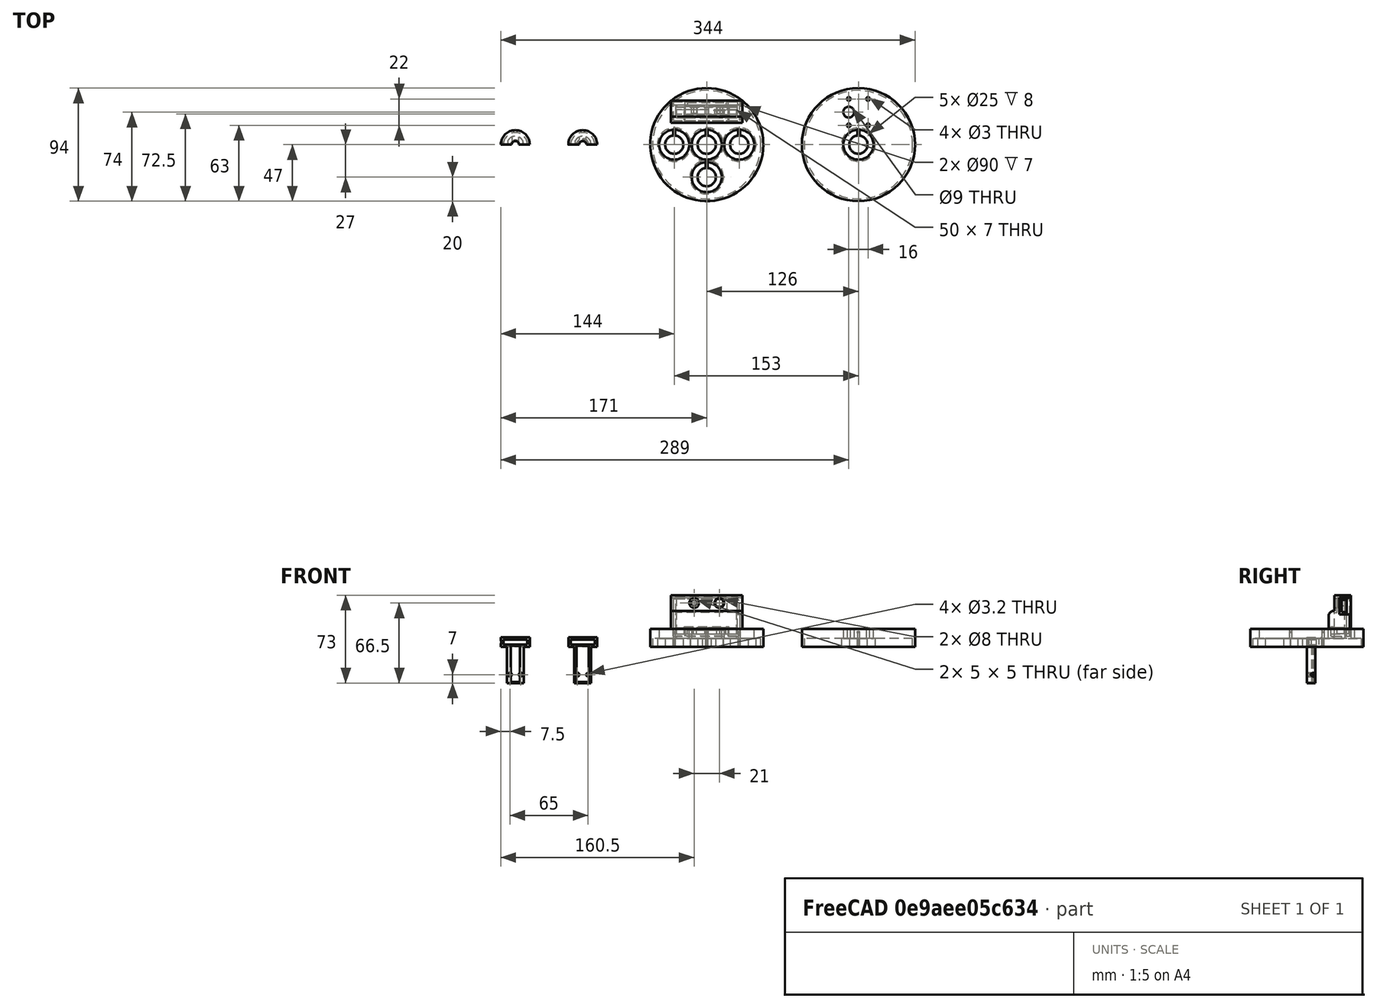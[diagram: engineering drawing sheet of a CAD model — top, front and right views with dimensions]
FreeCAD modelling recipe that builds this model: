
FCSTD DOCUMENT  (FreeCAD 0.21RUnknown)
Label: lidcup
License: All rights reserved
LicenseURL: https://en.wikipedia.org/wiki/All_rights_reserved
objects: PartDesign::SubtractiveCylinder×35, PartDesign::SubtractiveBox×18, PartDesign::AdditiveBox×17, PartDesign::AdditiveCylinder×13, PartDesign::Body×8, PartDesign::Fillet×1
note: 176 computed .brp shape members not serialized (recipe doc carries the construction recipe); baked Part::Feature solids carry a one-line shape summary decoded from their .brp

FEATURE [PartDesign::AdditiveCylinder] Cylinder
  Angle = 360
  AttacherType = Attacher::AttachEngine3D
  FirstAngle = 0
  Height = 15
  MapMode = 5
  Radius = 47
  SecondAngle = 0
  Support = -> [XY_Plane]
FEATURE [PartDesign::SubtractiveCylinder] Cylinder001
  Angle = 360
  AttacherType = Attacher::AttachEngine3D
  BaseFeature = -> Cylinder
  FirstAngle = 0
  Height = 7
  Radius = 45
  SecondAngle = 0
FEATURE [PartDesign::AdditiveCylinder] Cylinder003
  Angle = 360
  AttacherType = Attacher::AttachEngine3D
  BaseFeature = -> Cylinder001
  FirstAngle = 0
  Height = 10
  MapMode = 5
  Radius = 14
  SecondAngle = 0
  Support = -> [XY_Plane]
FEATURE [PartDesign::SubtractiveCylinder] Cylinder002
  Angle = 360
  AttacherType = Attacher::AttachEngine3D
  AttachmentOffset = pos=(0,0,7) rot=(0,0,1;0rad)
  BaseFeature = -> Cylinder003
  FirstAngle = 0
  Height = 8
  MapMode = 5
  Placement = pos=(0,0,7) rot=(0,0,1;0rad)
  Radius = 12.5
  SecondAngle = 0
  Support = -> [XY_Plane]
FEATURE [PartDesign::SubtractiveCylinder] Cylinder004
  Angle = 360
  AttacherType = Attacher::AttachEngine3D
  BaseFeature = -> Cylinder002
  FirstAngle = 0
  Height = 10
  Radius = 7.6
  SecondAngle = 0
FEATURE [PartDesign::SubtractiveBox] Box
  AttacherType = Attacher::AttachEngine3D
  AttachmentOffset = pos=(-0.75,0,0) rot=(0,0,1;0rad)
  BaseFeature = -> Cylinder004
  Height = 13
  Length = 1.5
  MapMode = 5
  Placement = pos=(-0.75,0,0) rot=(0,0,1;0rad)
  Support = -> [XY_Plane]
  Width = 13.3
FEATURE [PartDesign::SubtractiveCylinder] Cylinder005
  Angle = 360
  AttacherType = Attacher::AttachEngine3D
  AttachmentOffset = pos=(-8,38,0) rot=(0,0,1;0rad)
  BaseFeature = -> Box
  FirstAngle = 0
  Height = 15
  MapMode = 5
  Placement = pos=(-8,38,0) rot=(0,0,1;0rad)
  Radius = 1.5
  SecondAngle = 0
  Support = -> [XY_Plane]
FEATURE [PartDesign::SubtractiveCylinder] Cylinder006
  Angle = 360
  AttacherType = Attacher::AttachEngine3D
  AttachmentOffset = pos=(-8,16,0) rot=(0,0,1;0rad)
  BaseFeature = -> Cylinder005
  FirstAngle = 0
  Height = 15
  MapMode = 5
  Placement = pos=(-8,16,0) rot=(0,0,1;0rad)
  Radius = 1.5
  SecondAngle = 0
  Support = -> [XY_Plane]
FEATURE [PartDesign::SubtractiveCylinder] Cylinder007
  Angle = 360
  AttacherType = Attacher::AttachEngine3D
  AttachmentOffset = pos=(8,38,0) rot=(0,0,1;0rad)
  BaseFeature = -> Cylinder006
  FirstAngle = 0
  Height = 15
  MapMode = 5
  Placement = pos=(8,38,0) rot=(0,0,1;0rad)
  Radius = 1.5
  SecondAngle = 0
  Support = -> [XY_Plane]
FEATURE [PartDesign::SubtractiveCylinder] Cylinder008
  Angle = 360
  AttacherType = Attacher::AttachEngine3D
  AttachmentOffset = pos=(8,16,0) rot=(0,0,1;0rad)
  BaseFeature = -> Cylinder007
  FirstAngle = 0
  Height = 15
  MapMode = 5
  Placement = pos=(8,16,0) rot=(0,0,1;0rad)
  Radius = 1.5
  SecondAngle = 0
  Support = -> [XY_Plane]
FEATURE [PartDesign::SubtractiveCylinder] Cylinder009
  Angle = 360
  AttacherType = Attacher::AttachEngine3D
  AttachmentOffset = pos=(-8,27,0) rot=(0,0,1;0rad)
  BaseFeature = -> Cylinder008
  FirstAngle = 0
  Height = 15
  MapMode = 5
  Placement = pos=(-8,27,0) rot=(0,0,1;0rad)
  Radius = 4.5
  SecondAngle = 0
  Support = -> [XY_Plane]
FEATURE [PartDesign::Body] Body  label="Cup"
  Group = -> [Cylinder,Cylinder001,Cylinder003,Cylinder002,Cylinder004,Box,Cylinder005,Cylinder006,Cylinder007,Cylinder008,Cylinder009]
  Origin = -> Origin
  Tip = -> Cylinder009
FEATURE [PartDesign::AdditiveCylinder] Cylinder010
  Angle = 360
  AttacherType = Attacher::AttachEngine3D
  FirstAngle = 0
  Height = 15
  MapMode = 5
  Radius = 47
  SecondAngle = 0
  Support = -> [XY_Plane001]
FEATURE [PartDesign::SubtractiveCylinder] Cylinder011
  Angle = 360
  AttacherType = Attacher::AttachEngine3D
  BaseFeature = -> Cylinder010
  FirstAngle = 0
  Height = 7
  MapMode = 5
  Radius = 45
  SecondAngle = 0
  Support = -> [XY_Plane001]
FEATURE [PartDesign::AdditiveBox] Box002
  AttacherType = Attacher::AttachEngine3D
  Height = 1.5
  Length = 50
  MapMode = 5
  Support = -> [XY_Plane002]
  Width = 30
FEATURE [PartDesign::AdditiveBox] Box003
  AttacherType = Attacher::AttachEngine3D
  AttachmentOffset = pos=(42,18,0) rot=(0,0,1;0rad)
  BaseFeature = -> Box002
  Height = 4
  Length = 10
  MapMode = 5
  Placement = pos=(42,18,0) rot=(0,0,1;0rad)
  Support = -> [XY_Plane002]
  Width = 10
FEATURE [PartDesign::AdditiveCylinder] Cylinder017
  Angle = 360
  AttacherType = Attacher::AttachEngine3D
  BaseFeature = -> Cylinder011
  FirstAngle = 0
  Height = 10
  MapMode = 5
  Radius = 14
  SecondAngle = 0
  Support = -> [XY_Plane001]
FEATURE [PartDesign::SubtractiveCylinder] Cylinder013
  Angle = 360
  AttacherType = Attacher::AttachEngine3D
  AttachmentOffset = pos=(0,0,7) rot=(0,0,1;0rad)
  BaseFeature = -> Cylinder017
  FirstAngle = 0
  Height = 8
  MapMode = 5
  Placement = pos=(0,0,7) rot=(0,0,1;0rad)
  Radius = 12.5
  SecondAngle = 0
  Support = -> [XY_Plane001]
FEATURE [PartDesign::SubtractiveCylinder] Cylinder014
  Angle = 360
  AttacherType = Attacher::AttachEngine3D
  BaseFeature = -> Cylinder013
  FirstAngle = 0
  Height = 10
  MapMode = 5
  Radius = 7.6
  SecondAngle = 0
  Support = -> [XY_Plane001]
FEATURE [PartDesign::SubtractiveBox] Box001
  AttacherType = Attacher::AttachEngine3D
  AttachmentOffset = pos=(-0.75,0,0) rot=(0,0,1;0rad)
  BaseFeature = -> Cylinder014
  Height = 13
  Length = 1.5
  MapMode = 5
  Placement = pos=(-0.75,0,0) rot=(0,0,1;0rad)
  Support = -> [XY_Plane001]
  Width = 13.3
FEATURE [PartDesign::AdditiveCylinder] Cylinder015
  Angle = 360
  AttacherType = Attacher::AttachEngine3D
  AttachmentOffset = pos=(-27,0,0) rot=(0,0,1;0rad)
  BaseFeature = -> Box001
  FirstAngle = 0
  Height = 10
  MapMode = 5
  Placement = pos=(-27,0,0) rot=(0,0,1;0rad)
  Radius = 14
  SecondAngle = 0
  Support = -> [XY_Plane001]
FEATURE [PartDesign::AdditiveBox] Box004
  AttacherType = Attacher::AttachEngine3D
  AttachmentOffset = pos=(33,23,0) rot=(0,0,1;0rad)
  BaseFeature = -> Box003
  Height = 7
  Length = 5
  MapMode = 5
  Placement = pos=(33,23,0) rot=(0,0,1;0rad)
  Support = -> [XY_Plane002]
  Width = 5
FEATURE [PartDesign::AdditiveBox] Box005
  AttacherType = Attacher::AttachEngine3D
  AttachmentOffset = pos=(12,23,0) rot=(0,0,1;0rad)
  BaseFeature = -> Box004
  Height = 7
  Length = 5
  MapMode = 5
  Placement = pos=(12,23,0) rot=(0,0,1;0rad)
  Support = -> [XY_Plane002]
  Width = 5
FEATURE [PartDesign::AdditiveBox] Box006
  AttacherType = Attacher::AttachEngine3D
  AttachmentOffset = pos=(7,0,0) rot=(0,0,1;0rad)
  BaseFeature = -> Box005
  Height = 8
  Length = 7
  MapMode = 5
  Placement = pos=(7,0,0) rot=(0,0,1;0rad)
  Support = -> [XY_Plane002]
  Width = 5
FEATURE [PartDesign::AdditiveBox] Box007
  AttacherType = Attacher::AttachEngine3D
  AttachmentOffset = pos=(16.5,0,0) rot=(0,0,1;0rad)
  BaseFeature = -> Box006
  Height = 8
  Length = 7
  MapMode = 5
  Placement = pos=(16.5,0,0) rot=(0,0,1;0rad)
  Support = -> [XY_Plane002]
  Width = 5
FEATURE [PartDesign::AdditiveBox] Box008
  AttacherType = Attacher::AttachEngine3D
  AttachmentOffset = pos=(26.5,0,0) rot=(0,0,1;0rad)
  BaseFeature = -> Box007
  Height = 8
  Length = 7
  MapMode = 5
  Placement = pos=(26.5,0,0) rot=(0,0,1;0rad)
  Support = -> [XY_Plane002]
  Width = 5
FEATURE [PartDesign::AdditiveBox] Box009
  AttacherType = Attacher::AttachEngine3D
  AttachmentOffset = pos=(36,0,0) rot=(0,0,1;0rad)
  BaseFeature = -> Box008
  Height = 8
  Length = 7
  MapMode = 5
  Placement = pos=(36,0,0) rot=(0,0,1;0rad)
  Support = -> [XY_Plane002]
  Width = 5
FEATURE [PartDesign::SubtractiveCylinder] Cylinder019
  Angle = 360
  AttacherType = Attacher::AttachEngine3D
  AttachmentOffset = pos=(-27,0,7) rot=(0,0,1;0rad)
  BaseFeature = -> Cylinder015
  FirstAngle = 0
  Height = 8
  MapMode = 5
  Placement = pos=(-27,0,7) rot=(0,0,1;0rad)
  Radius = 12.5
  SecondAngle = 0
  Support = -> [XY_Plane001]
FEATURE [PartDesign::SubtractiveCylinder] Cylinder020
  Angle = 360
  AttacherType = Attacher::AttachEngine3D
  AttachmentOffset = pos=(-27,0,0) rot=(0,0,1;0rad)
  BaseFeature = -> Cylinder019
  FirstAngle = 0
  Height = 10
  MapMode = 5
  Placement = pos=(-27,0,0) rot=(0,0,1;0rad)
  Radius = 7.6
  SecondAngle = 0
  Support = -> [XY_Plane001]
FEATURE [PartDesign::SubtractiveBox] Box012
  AttacherType = Attacher::AttachEngine3D
  AttachmentOffset = pos=(-27.75,0,0) rot=(0,0,1;0rad)
  BaseFeature = -> Cylinder020
  Height = 13
  Length = 1.5
  MapMode = 5
  Placement = pos=(-27.75,0,0) rot=(0,0,1;0rad)
  Support = -> [XY_Plane001]
  Width = 13.3
FEATURE [PartDesign::AdditiveCylinder] Cylinder016
  Angle = 360
  AttacherType = Attacher::AttachEngine3D
  AttachmentOffset = pos=(27,0,0) rot=(0,0,1;0rad)
  BaseFeature = -> Box012
  FirstAngle = 0
  Height = 10
  MapMode = 5
  Placement = pos=(27,0,0) rot=(0,0,1;0rad)
  Radius = 14
  SecondAngle = 0
  Support = -> [XY_Plane001]
FEATURE [PartDesign::SubtractiveCylinder] Cylinder021
  Angle = 360
  AttacherType = Attacher::AttachEngine3D
  AttachmentOffset = pos=(27,0,7) rot=(0,0,1;0rad)
  BaseFeature = -> Cylinder016
  FirstAngle = 0
  Height = 8
  MapMode = 5
  Placement = pos=(27,0,7) rot=(0,0,1;0rad)
  Radius = 12.5
  SecondAngle = 0
  Support = -> [XY_Plane001]
FEATURE [PartDesign::SubtractiveCylinder] Cylinder022
  Angle = 360
  AttacherType = Attacher::AttachEngine3D
  AttachmentOffset = pos=(27,0,0) rot=(0,0,1;0rad)
  BaseFeature = -> Cylinder021
  FirstAngle = 0
  Height = 10
  MapMode = 5
  Placement = pos=(27,0,0) rot=(0,0,1;0rad)
  Radius = 7.6
  SecondAngle = 0
  Support = -> [XY_Plane001]
FEATURE [PartDesign::SubtractiveBox] Box013
  AttacherType = Attacher::AttachEngine3D
  AttachmentOffset = pos=(26.25,0,0) rot=(0,0,1;0rad)
  BaseFeature = -> Cylinder022
  Height = 13
  Length = 1.5
  MapMode = 5
  Placement = pos=(26.25,0,0) rot=(0,0,1;0rad)
  Support = -> [XY_Plane001]
  Width = 13.3
FEATURE [PartDesign::AdditiveCylinder] Cylinder018
  Angle = 360
  AttacherType = Attacher::AttachEngine3D
  AttachmentOffset = pos=(0,-27,0) rot=(0,0,1;0rad)
  BaseFeature = -> Box013
  FirstAngle = 0
  Height = 10
  MapMode = 5
  Placement = pos=(0,-27,0) rot=(0,0,1;0rad)
  Radius = 14
  SecondAngle = 0
  Support = -> [XY_Plane001]
FEATURE [PartDesign::SubtractiveCylinder] Cylinder023
  Angle = 360
  AttacherType = Attacher::AttachEngine3D
  AttachmentOffset = pos=(0,-27,7) rot=(0,0,1;0rad)
  BaseFeature = -> Cylinder018
  FirstAngle = 0
  Height = 8
  MapMode = 5
  Placement = pos=(0,-27,7) rot=(0,0,1;0rad)
  Radius = 12.5
  SecondAngle = 0
  Support = -> [XY_Plane001]
FEATURE [PartDesign::SubtractiveCylinder] Cylinder024
  Angle = 360
  AttacherType = Attacher::AttachEngine3D
  AttachmentOffset = pos=(0,-27,0) rot=(0,0,1;0rad)
  BaseFeature = -> Cylinder023
  FirstAngle = 0
  Height = 10
  MapMode = 5
  Placement = pos=(0,-27,0) rot=(0,0,1;0rad)
  Radius = 7.6
  SecondAngle = 0
  Support = -> [XY_Plane001]
FEATURE [PartDesign::SubtractiveBox] Box014
  AttacherType = Attacher::AttachEngine3D
  AttachmentOffset = pos=(-0.75,-27,0) rot=(0,0,1;0rad)
  BaseFeature = -> Cylinder024
  Height = 13
  Length = 1.5
  MapMode = 5
  Placement = pos=(-0.75,-27,0) rot=(0,0,1;0rad)
  Support = -> [XY_Plane001]
  Width = 13.3
FEATURE [PartDesign::SubtractiveBox] Box010
  AttacherType = Attacher::AttachEngine3D
  AttachmentOffset = pos=(-28,20,9) rot=(0,0,1;0rad)
  BaseFeature = -> Box014
  Height = 6
  Length = 56
  MapMode = 5
  Placement = pos=(-28,20,9) rot=(0,0,1;0rad)
  Support = -> [XY_Plane001]
  Width = 16
FEATURE [PartDesign::SubtractiveBox] Box011
  AttacherType = Attacher::AttachEngine3D
  AttachmentOffset = pos=(-25,22,0) rot=(0,0,1;0rad)
  BaseFeature = -> Box010
  Height = 10
  Length = 50
  MapMode = 5
  Placement = pos=(-25,22,0) rot=(0,0,1;0rad)
  Support = -> [XY_Plane001]
  Width = 7
FEATURE [PartDesign::Body] Body001  label="Cup 4"
  Group = -> [Cylinder010,Cylinder011,Cylinder017,Cylinder013,Cylinder014,Box001,Cylinder015,Cylinder019,Cylinder020,Box012,Cylinder016,Cylinder021,Cylinder022,Box013,Cylinder018,Cylinder023,Cylinder024,Box014,Box010,Box011]
  Origin = -> Origin001
  Placement = pos=(-126,0,0) rot=(0,0,1;0rad)
  Tip = -> Box011
FEATURE [PartDesign::AdditiveCylinder] Cylinder025
  Angle = 360
  AttacherType = Attacher::AttachEngine3D
  FirstAngle = 0
  Height = 8
  MapMode = 5
  Radius = 12
  SecondAngle = 0
  Support = -> [XY_Plane003]
FEATURE [PartDesign::AdditiveCylinder] Cylinder026
  Angle = 360
  AttacherType = Attacher::AttachEngine3D
  AttachmentOffset = pos=(0,0,-30) rot=(0,0,1;0rad)
  BaseFeature = -> Cylinder025
  FirstAngle = 0
  Height = 30
  MapMode = 5
  Placement = pos=(0,0,-30) rot=(0,0,1;0rad)
  Radius = 7
  SecondAngle = 0
  Support = -> [XY_Plane003]
FEATURE [PartDesign::SubtractiveBox] Box015
  AttacherType = Attacher::AttachEngine3D
  AttachmentOffset = pos=(-12,-12,-30) rot=(0,0,1;0rad)
  BaseFeature = -> Cylinder026
  Height = 38
  Length = 24
  MapMode = 5
  Placement = pos=(-12,-12,-30) rot=(0,0,1;0rad)
  Support = -> [XY_Plane003]
  Width = 12
FEATURE [PartDesign::SubtractiveCylinder] Cylinder027
  Angle = 360
  AttacherType = Attacher::AttachEngine3D
  AttachmentOffset = pos=(0,0,-29) rot=(0,0,1;0rad)
  BaseFeature = -> Box015
  FirstAngle = 0
  Height = 30
  MapMode = 5
  Placement = pos=(0,0,-29) rot=(0,0,1;0rad)
  Radius = 5
  SecondAngle = 0
  Support = -> [XY_Plane003]
FEATURE [PartDesign::SubtractiveCylinder] Cylinder028
  Angle = 360
  AttacherType = Attacher::AttachEngine3D
  AttachmentOffset = pos=(0,0,-30) rot=(0,0,1;0rad)
  BaseFeature = -> Cylinder027
  FirstAngle = 0
  Height = 1
  MapMode = 5
  Placement = pos=(0,0,-30) rot=(0,0,1;0rad)
  Radius = 4.5
  SecondAngle = 0
  Support = -> [XY_Plane003]
FEATURE [PartDesign::SubtractiveCylinder] Cylinder032
  Angle = 360
  AttacherType = Attacher::AttachEngine3D
  AttachmentOffset = pos=(0,0,1) rot=(0,0,1;0rad)
  BaseFeature = -> Cylinder028
  FirstAngle = 0
  Height = 1
  MapMode = 5
  Placement = pos=(0,0,1) rot=(0,0,1;0rad)
  Radius = 4.5
  SecondAngle = 0
  Support = -> [XY_Plane003]
FEATURE [PartDesign::SubtractiveCylinder] Cylinder029
  Angle = 360
  AttacherType = Attacher::AttachEngine3D
  AttachmentOffset = pos=(0,0,2) rot=(0,0,1;0rad)
  BaseFeature = -> Cylinder032
  FirstAngle = 0
  Height = 4
  MapMode = 5
  Placement = pos=(0,0,2) rot=(0,0,1;0rad)
  Radius = 10
  SecondAngle = 0
  Support = -> [XY_Plane003]
FEATURE [PartDesign::SubtractiveCylinder] Cylinder030
  Angle = 360
  AttacherType = Attacher::AttachEngine3D
  AttachmentOffset = pos=(0,0,6) rot=(0,0,1;0rad)
  BaseFeature = -> Cylinder029
  FirstAngle = 0
  Height = 2
  MapMode = 5
  Placement = pos=(0,0,6) rot=(0,0,1;0rad)
  Radius = 3
  SecondAngle = 0
  Support = -> [XY_Plane003]
FEATURE [PartDesign::SubtractiveCylinder] Cylinder031
  Angle = 360
  AttacherType = Attacher::AttachEngine3D
  AttachmentOffset = pos=(0,4,-12) rot=(0,0,1;0rad)
  BaseFeature = -> Cylinder030
  FirstAngle = 0
  Height = 10
  MapMode = 5
  Placement = pos=(-12,3.6e-15,4) rot=(0.57735,0.57735,0.57735;2.0944rad)
  Radius = 1.4
  SecondAngle = 0
  Support = -> [YZ_Plane003]
FEATURE [PartDesign::AdditiveBox] Box016
  AttacherType = Attacher::AttachEngine3D
  AttachmentOffset = pos=(9,0,-2) rot=(0,0,1;0rad)
  BaseFeature = -> Box009
  Height = 2
  Length = 32
  MapMode = 5
  Placement = pos=(9,0,-2) rot=(0,0,1;0rad)
  Support = -> [XY_Plane002]
  Width = 3
FEATURE [PartDesign::Body] Body002  label="PCB"
  Group = -> [Box002,Box003,Box004,Box005,Box006,Box007,Box008,Box009,Box016]
  Origin = -> Origin002
  Placement = pos=(-151,33,11) rot=(1,0,0;1.5708rad)
  Tip = -> Box016
FEATURE [PartDesign::AdditiveBox] Box017
  AttacherType = Attacher::AttachEngine3D
  Height = 32
  Length = 55.2
  MapMode = 5
  Support = -> [XY_Plane004]
  Width = 2.5
FEATURE [PartDesign::SubtractiveBox] Box018
  AttacherType = Attacher::AttachEngine3D
  AttachmentOffset = pos=(9.5,0,0) rot=(0,0,1;0rad)
  BaseFeature = -> Box017
  Height = 7
  Length = 36
  MapMode = 5
  Placement = pos=(9.5,0,0) rot=(0,0,1;0rad)
  Support = -> [XY_Plane004]
  Width = 3
FEATURE [PartDesign::AdditiveBox] Box023
  AttacherType = Attacher::AttachEngine3D
  Height = 4
  Length = 55.2
  MapMode = 5
  Support = -> [XY_Plane005]
  Width = 13
FEATURE [PartDesign::AdditiveBox] Box024
  AttacherType = Attacher::AttachEngine3D
  AttachmentOffset = pos=(-2,-2,4) rot=(0,0,1;0rad)
  BaseFeature = -> Box023
  Height = 28
  Length = 59.2
  MapMode = 5
  Placement = pos=(-2,-2,4) rot=(0,0,1;0rad)
  Support = -> [XY_Plane005]
  Width = 17.5
FEATURE [PartDesign::SubtractiveBox] Box025
  AttacherType = Attacher::AttachEngine3D
  AttachmentOffset = pos=(9,0,0) rot=(0,0,1;0rad)
  BaseFeature = -> Box024
  Height = 6
  Length = 37
  MapMode = 5
  Placement = pos=(9,0,0) rot=(0,0,1;0rad)
  Support = -> [XY_Plane005]
  Width = 13
FEATURE [PartDesign::SubtractiveBox] Box026
  AttacherType = Attacher::AttachEngine3D
  AttachmentOffset = pos=(2,11,0) rot=(0,0,1;0rad)
  BaseFeature = -> Box025
  Height = 30.5
  Length = 51
  MapMode = 5
  Placement = pos=(2,11,0) rot=(0,0,1;0rad)
  Support = -> [XY_Plane005]
  Width = 2
FEATURE [PartDesign::SubtractiveBox] Box027
  AttacherType = Attacher::AttachEngine3D
  AttachmentOffset = pos=(2,3,5) rot=(0,0,1;0rad)
  BaseFeature = -> Box026
  Height = 12.5
  Length = 51
  MapMode = 5
  Placement = pos=(2,3,5) rot=(0,0,1;0rad)
  Support = -> [XY_Plane005]
  Width = 8
FEATURE [PartDesign::SubtractiveBox] Box028
  AttacherType = Attacher::AttachEngine3D
  AttachmentOffset = pos=(-2,-2,19) rot=(0,0,1;0rad)
  BaseFeature = -> Box027
  Height = 13
  Length = 59.2
  MapMode = 5
  Placement = pos=(-2,-2,19) rot=(0,0,1;0rad)
  Support = -> [XY_Plane005]
  Width = 5
FEATURE [PartDesign::SubtractiveBox] Box029
  AttacherType = Attacher::AttachEngine3D
  AttachmentOffset = pos=(2,5,17) rot=(0,0,1;0rad)
  BaseFeature = -> Box028
  Height = 13
  Length = 51
  MapMode = 5
  Placement = pos=(2,5,17) rot=(0,0,1;0rad)
  Support = -> [XY_Plane005]
  Width = 8
FEATURE [PartDesign::SubtractiveCylinder] Cylinder033
  Angle = 360
  AttacherType = Attacher::AttachEngine3D
  AttachmentOffset = pos=(17.1,25.5,-5) rot=(0,0,1;0rad)
  BaseFeature = -> Box029
  FirstAngle = 0
  Height = 3
  MapMode = 5
  Placement = pos=(17.1,5,25.5) rot=(1,0,0;1.5708rad)
  Radius = 4
  SecondAngle = 0
  Support = -> [XZ_Plane005]
FEATURE [PartDesign::SubtractiveCylinder] Cylinder034
  Angle = 360
  AttacherType = Attacher::AttachEngine3D
  AttachmentOffset = pos=(38.1,25.5,-5) rot=(0,0,1;0rad)
  BaseFeature = -> Cylinder033
  FirstAngle = 0
  Height = 3
  MapMode = 5
  Placement = pos=(38.1,5,25.5) rot=(1,0,0;1.5708rad)
  Radius = 4
  SecondAngle = 0
  Support = -> [XZ_Plane005]
FEATURE [PartDesign::SubtractiveBox] Box030
  AttacherType = Attacher::AttachEngine3D
  AttachmentOffset = pos=(53,7,16) rot=(0,0,1;0rad)
  BaseFeature = -> Cylinder034
  Height = 14
  Length = 5
  MapMode = 5
  Placement = pos=(53,7,16) rot=(0,0,1;0rad)
  Support = -> [XY_Plane005]
  Width = 8.5
FEATURE [PartDesign::SubtractiveBox] Box031
  AttacherType = Attacher::AttachEngine3D
  AttachmentOffset = pos=(0,13,4) rot=(0,0,1;0rad)
  BaseFeature = -> Box030
  Height = 25
  Length = 55.2
  MapMode = 5
  Placement = pos=(0,13,4) rot=(0,0,1;0rad)
  Support = -> [XY_Plane005]
  Width = 2.5
FEATURE [PartDesign::SubtractiveCylinder] Cylinder035
  Angle = 360
  AttacherType = Attacher::AttachEngine3D
  AttachmentOffset = pos=(4.5,-23,-7) rot=(0,0,1;0rad)
  BaseFeature = -> Cylinder031
  FirstAngle = 0
  Height = 7
  MapMode = 5
  Placement = pos=(4.5,7,-23) rot=(1,0,0;1.5708rad)
  Radius = 1.6
  SecondAngle = 0
  Support = -> [XZ_Plane003]
FEATURE [PartDesign::SubtractiveCylinder] Cylinder036
  Angle = 360
  AttacherType = Attacher::AttachEngine3D
  AttachmentOffset = pos=(-4.5,-23,-7) rot=(0,0,1;0rad)
  BaseFeature = -> Cylinder035
  FirstAngle = 0
  Height = 7
  MapMode = 5
  Placement = pos=(-4.5,7,-23) rot=(1,0,0;1.5708rad)
  Radius = 1.6
  SecondAngle = 0
  Support = -> [XZ_Plane003]
FEATURE [PartDesign::Body] Body003  label="Cotton Holder 10"
  Group = -> [Cylinder025,Cylinder026,Box015,Cylinder027,Cylinder028,Cylinder032,Cylinder029,Cylinder030,Cylinder031,Cylinder035,Cylinder036]
  Origin = -> Origin003
  Placement = pos=(-229,0,0) rot=(0,0,1;0rad)
  Tip = -> Cylinder036
FEATURE [PartDesign::AdditiveCylinder] Cylinder037
  Angle = 360
  AttacherType = Attacher::AttachEngine3D
  FirstAngle = 0
  Height = 5
  MapMode = 5
  Placement = pos=(0,0,0) rot=(1,0,0;1.5708rad)
  Radius = 3.75
  SecondAngle = 0
  Support = -> [XZ_Plane006]
FEATURE [PartDesign::AdditiveCylinder] Cylinder038
  Angle = 360
  AttacherType = Attacher::AttachEngine3D
  AttachmentOffset = pos=(0,0,-0.8) rot=(0,0,1;0rad)
  BaseFeature = -> Cylinder037
  FirstAngle = 0
  Height = 0.8
  MapMode = 5
  Placement = pos=(0,0.8,2e-16) rot=(1,0,0;1.5708rad)
  Radius = 4.4
  SecondAngle = 0
  Support = -> [XZ_Plane006]
FEATURE [PartDesign::Body] Body006  label="Button"
  Group = -> [Cylinder037,Cylinder038]
  Origin = -> Origin006
  Placement = pos=(-115.5,28.1,36.5) rot=(0,0,1;0rad)
  Tip = -> Cylinder038
FEATURE [PartDesign::SubtractiveBox] Box032
  AttacherType = Attacher::AttachEngine3D
  AttachmentOffset = pos=(0,0,31) rot=(0,0,1;0rad)
  BaseFeature = -> Box018
  Height = 1
  Length = 53
  MapMode = 5
  Placement = pos=(0,0,31) rot=(0,0,1;0rad)
  Support = -> [XY_Plane004]
  Width = 2.5
FEATURE [PartDesign::AdditiveBox] Box019
  AttacherType = Attacher::AttachEngine3D
  AttachmentOffset = pos=(-2,2.5,6) rot=(0,0,1;0rad)
  BaseFeature = -> Box032
  Height = 26
  Length = 59.2
  MapMode = 5
  Placement = pos=(-2,2.5,6) rot=(0,0,1;0rad)
  Support = -> [XY_Plane004]
  Width = 1
FEATURE [PartDesign::AdditiveBox] Box020
  AttacherType = Attacher::AttachEngine3D
  AttachmentOffset = pos=(0,-13,0) rot=(0,0,1;0rad)
  BaseFeature = -> Box019
  Height = 2
  Length = 9.5
  MapMode = 5
  Placement = pos=(0,-13,0) rot=(0,0,1;0rad)
  Support = -> [XY_Plane004]
  Width = 13
FEATURE [PartDesign::AdditiveBox] Box021
  AttacherType = Attacher::AttachEngine3D
  AttachmentOffset = pos=(45.5,-13,0) rot=(0,0,1;0rad)
  BaseFeature = -> Box020
  Height = 2
  Length = 9.5
  MapMode = 5
  Placement = pos=(45.5,-13,0) rot=(0,0,1;0rad)
  Support = -> [XY_Plane004]
  Width = 13
FEATURE [PartDesign::AdditiveBox] Box033
  AttacherType = Attacher::AttachEngine3D
  AttachmentOffset = pos=(55.2,0,18) rot=(0,0,1;0rad)
  BaseFeature = -> Box021
  Height = 14
  Length = 2
  MapMode = 5
  Placement = pos=(55.2,0,18) rot=(0,0,1;0rad)
  Support = -> [XY_Plane004]
  Width = 2.5
FEATURE [PartDesign::Body] Body004  label="PCB Shell Back"
  Group = -> [Box017,Box018,Box032,Box019,Box020,Box021,Box033]
  Origin = -> Origin004
  Placement = pos=(-153.6,33.1,9) rot=(0,0,1;0rad)
  Tip = -> Box033
FEATURE [PartDesign::AdditiveBox] Box034
  AttacherType = Attacher::AttachEngine3D
  AttachmentOffset = pos=(-2,30,-16.5) rot=(0,0,1;0rad)
  BaseFeature = -> Box031
  Height = 1
  Length = 59.2
  MapMode = 5
  Placement = pos=(-2,16.5,30) rot=(1,0,0;1.5708rad)
  Support = -> [XZ_Plane004]
  Width = 2
FEATURE [PartDesign::Fillet] Fillet
  Base = -> Box034 [Edge9]
  BaseFeature = -> Box034
  Placement = pos=(-2,16.5,30) rot=(1,0,0;1.5708rad)
  Radius = 4.5
  SupportTransform = false
  UseAllEdges = false
FEATURE [PartDesign::Body] Body005  label="PCB Shell Front"
  Group = -> [Box023,Box024,Box025,Box026,Box027,Box028,Box029,Cylinder033,Cylinder034,Box030,Box031,Box034,Fillet]
  Origin = -> Origin005
  Placement = pos=(-153.6,20.1,11) rot=(0,0,1;0rad)
  Tip = -> Fillet
FEATURE [PartDesign::AdditiveCylinder] Cylinder039
  Angle = 360
  AttacherType = Attacher::AttachEngine3D
  FirstAngle = 0
  Height = 8
  MapMode = 5
  Radius = 12
  SecondAngle = 0
  Support = -> [XY_Plane007]
FEATURE [PartDesign::AdditiveCylinder] Cylinder040
  Angle = 360
  AttacherType = Attacher::AttachEngine3D
  AttachmentOffset = pos=(0,0,-30) rot=(0,0,1;0rad)
  BaseFeature = -> Cylinder039
  FirstAngle = 0
  Height = 30
  MapMode = 5
  Placement = pos=(0,0,-30) rot=(0,0,1;0rad)
  Radius = 7
  SecondAngle = 0
  Support = -> [XY_Plane007]
FEATURE [PartDesign::SubtractiveBox] Box035
  AttacherType = Attacher::AttachEngine3D
  AttachmentOffset = pos=(-12,-12,-30) rot=(0,0,1;0rad)
  BaseFeature = -> Cylinder040
  Height = 38
  Length = 24
  MapMode = 5
  Placement = pos=(-12,-12,-30) rot=(0,0,1;0rad)
  Support = -> [XY_Plane007]
  Width = 12
FEATURE [PartDesign::SubtractiveCylinder] Cylinder041
  Angle = 360
  AttacherType = Attacher::AttachEngine3D
  AttachmentOffset = pos=(0,0,-29) rot=(0,0,1;0rad)
  BaseFeature = -> Box035
  FirstAngle = 0
  Height = 30
  MapMode = 5
  Placement = pos=(0,0,-29) rot=(0,0,1;0rad)
  Radius = 3.75
  SecondAngle = 0
  Support = -> [XY_Plane007]
FEATURE [PartDesign::SubtractiveCylinder] Cylinder042
  Angle = 360
  AttacherType = Attacher::AttachEngine3D
  AttachmentOffset = pos=(0,0,-30) rot=(0,0,1;0rad)
  BaseFeature = -> Cylinder041
  FirstAngle = 0
  Height = 1
  MapMode = 5
  Placement = pos=(0,0,-30) rot=(0,0,1;0rad)
  Radius = 3
  SecondAngle = 0
  Support = -> [XY_Plane007]
FEATURE [PartDesign::SubtractiveCylinder] Cylinder046
  Angle = 360
  AttacherType = Attacher::AttachEngine3D
  AttachmentOffset = pos=(0,0,1) rot=(0,0,1;0rad)
  BaseFeature = -> Cylinder042
  FirstAngle = 0
  Height = 1
  MapMode = 5
  Placement = pos=(0,0,1) rot=(0,0,1;0rad)
  Radius = 3
  SecondAngle = 0
  Support = -> [XY_Plane007]
FEATURE [PartDesign::SubtractiveCylinder] Cylinder043
  Angle = 360
  AttacherType = Attacher::AttachEngine3D
  AttachmentOffset = pos=(0,0,2) rot=(0,0,1;0rad)
  BaseFeature = -> Cylinder046
  FirstAngle = 0
  Height = 4
  MapMode = 5
  Placement = pos=(0,0,2) rot=(0,0,1;0rad)
  Radius = 10
  SecondAngle = 0
  Support = -> [XY_Plane007]
FEATURE [PartDesign::SubtractiveCylinder] Cylinder044
  Angle = 360
  AttacherType = Attacher::AttachEngine3D
  AttachmentOffset = pos=(0,0,6) rot=(0,0,1;0rad)
  BaseFeature = -> Cylinder043
  FirstAngle = 0
  Height = 2
  MapMode = 5
  Placement = pos=(0,0,6) rot=(0,0,1;0rad)
  Radius = 3
  SecondAngle = 0
  Support = -> [XY_Plane003]
FEATURE [PartDesign::SubtractiveCylinder] Cylinder045
  Angle = 360
  AttacherType = Attacher::AttachEngine3D
  AttachmentOffset = pos=(0.7,4,-12) rot=(0,0,1;0rad)
  BaseFeature = -> Cylinder044
  FirstAngle = 0
  Height = 10
  MapMode = 5
  Placement = pos=(-12,0.7,4) rot=(0.57735,0.57735,0.57735;2.0944rad)
  Radius = 1.4
  SecondAngle = 0
  Support = -> [YZ_Plane007]
FEATURE [PartDesign::SubtractiveCylinder] Cylinder047
  Angle = 360
  AttacherType = Attacher::AttachEngine3D
  AttachmentOffset = pos=(4.5,-23,-7) rot=(0,0,1;0rad)
  BaseFeature = -> Cylinder045
  FirstAngle = 0
  Height = 7
  MapMode = 5
  Placement = pos=(4.5,7,-23) rot=(1,0,0;1.5708rad)
  Radius = 1.6
  SecondAngle = 0
  Support = -> [XZ_Plane007]
FEATURE [PartDesign::SubtractiveCylinder] Cylinder048
  Angle = 360
  AttacherType = Attacher::AttachEngine3D
  AttachmentOffset = pos=(-4.5,-23,-7) rot=(0,0,1;0rad)
  BaseFeature = -> Cylinder047
  FirstAngle = 0
  Height = 7
  MapMode = 5
  Placement = pos=(-4.5,7,-23) rot=(1,0,0;1.5708rad)
  Radius = 1.6
  SecondAngle = 0
  Support = -> [XZ_Plane007]
FEATURE [PartDesign::Body] Body007  label="Cotton Holder 8"
  Group = -> [Cylinder039,Cylinder040,Box035,Cylinder041,Cylinder042,Cylinder046,Cylinder043,Cylinder044,Cylinder045,Cylinder047,Cylinder048]
  Origin = -> Origin007
  Placement = pos=(-285,0,0) rot=(0,0,1;0rad)
  Tip = -> Cylinder048
